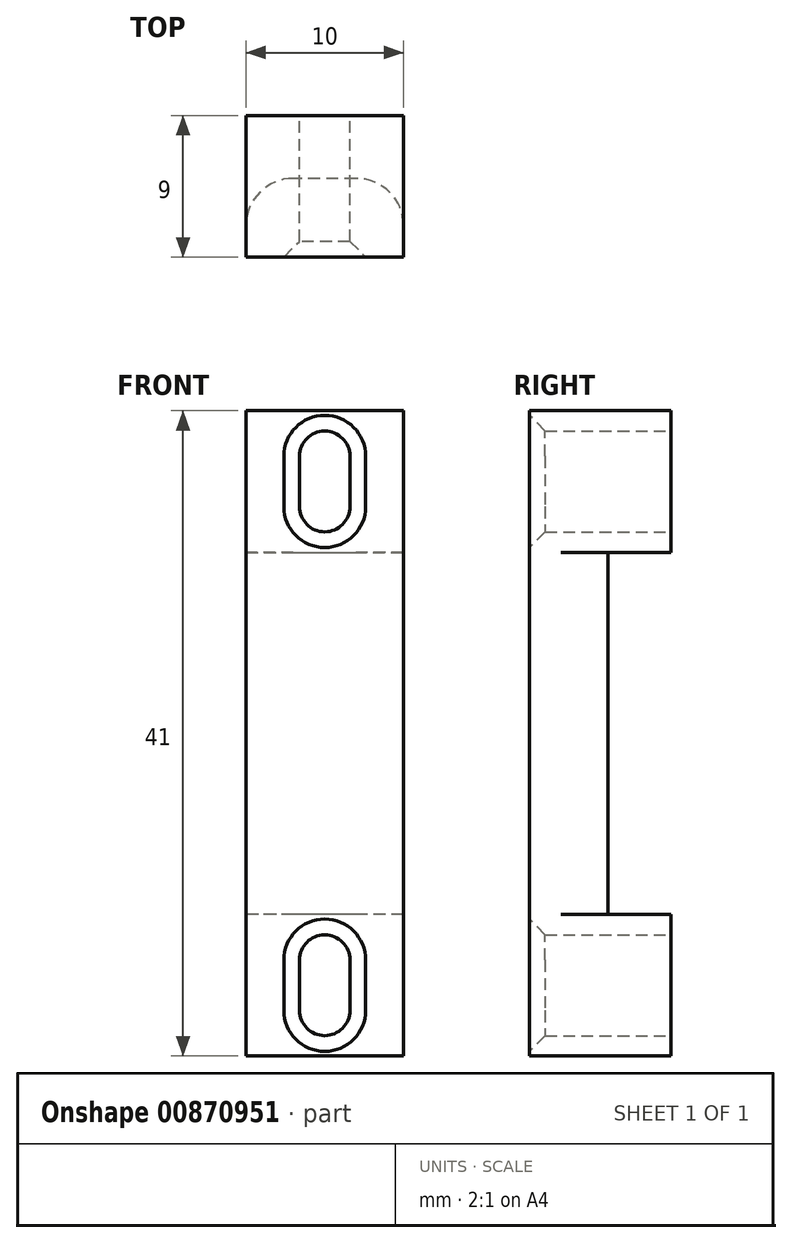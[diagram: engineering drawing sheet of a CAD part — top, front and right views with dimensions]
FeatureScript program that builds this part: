
annotation { "Feature Type Name" : "Feature", "Feature Type Description" : "" }
export const myFeature = defineFeature(function(context is Context, id is Id, definition is map)
    precondition{}
    {
        {
            var Q0;
            Q0=qCreatedBy(makeId("Front.planeOp"),FACE);
            var sketch = newSketch(context, id + "F0", { "sketchPlane" : qUnion([Q0])});
            skLineSegment(sketch, "E0.bottom", {"start": v(0, 0) * mm, "end": v(10, 0) * mm});
            skLineSegment(sketch, "E0.top", {"start": v(0, 41) * mm, "end": v(10, 41) * mm});
            skLineSegment(sketch, "E0.left", {"start": v(0, 0) * mm, "end": v(0, 41) * mm});
            skLineSegment(sketch, "E0.right", {"start": v(10, 0) * mm, "end": v(10, 41) * mm});
            skLineSegment(sketch, "E1", {"start": v(10, 20.5) * mm, "end": v(0, 20.5) * mm, "construction": true});
            skLineSegment(sketch, "E2", {"start": v(5, 20.5) * mm, "end": v(5, 36.5) * mm, "construction": true});
            skLineSegment(sketch, "E3", {"start": v(5, 20.5) * mm, "end": v(5, 4.5) * mm, "construction": true});
            skArc(sketch, "E4", {"start": v(3.4, 34.9) * mm, "mid": v(5, 33.3) * mm, "end": v(6.6, 34.9) * mm});
            skArc(sketch, "E5", {"start": v(6.6, 38.1) * mm, "mid": v(5, 39.7) * mm, "end": v(3.4, 38.1) * mm});
            skLineSegment(sketch, "E6", {"start": v(3.4, 38.1) * mm, "end": v(3.4, 34.9) * mm});
            skLineSegment(sketch, "E7", {"start": v(6.6, 38.1) * mm, "end": v(6.6, 34.9) * mm});
            skArc(sketch, "E8", {"start": v(6.6, 6.1) * mm, "mid": v(5, 7.7) * mm, "end": v(3.4, 6.1) * mm});
            skArc(sketch, "E9", {"start": v(3.4, 2.9) * mm, "mid": v(5, 1.3) * mm, "end": v(6.6, 2.9) * mm});
            skPoint(sketch, "E9.centerSnap0", {"position": v(5, 0) * mm});
            skLineSegment(sketch, "E10", {"start": v(3.4, 6.1) * mm, "end": v(3.4, 2.9) * mm});
            skLineSegment(sketch, "E11", {"start": v(6.6, 6.1) * mm, "end": v(6.6, 2.9) * mm});
            skSolve(sketch);
        }
        {
            var Q0;
            Q0=makeQuery(id+"F0.imprint","IMPRINT",FACE,{"disambiguationData":[TD([[makeQuery(id+"F0.imprint","IMPRINT",EDGE,{"derivedFrom":sQuery(id+"F0.wireOp",EDGE,"E0.bottom")}),1.0]])]});
            extrude(context, id + "F1", {"entities" : qUnion([Q0]), "depth" : 5 * mm, "offsetDistance" : 25 * mm});
        }
        {
            var Q0;
            Q0=qCreatedBy(makeId("Top.planeOp"),FACE);
            cPlane(context, id + "F2", {"entities" : qUnion([Q0]), "cplaneType" : CPlaneType.OFFSET, "offset" : 9 * mm, "width" : 150 * mm, "height" : 150 * mm});
        }
        {
            var Q0;
            Q0=qCreatedBy(id+"F2.planeOp",FACE);
            var sketch = newSketch(context, id + "F3", { "sketchPlane" : qUnion([Q0])});
            skLineSegment(sketch, "E12.0", {"start": v(3, 0) * mm, "end": v(7, 0) * mm});
            skPoint(sketch, "E13.0", {"position": v(10, -2.5) * mm});
            skLineSegment(sketch, "E14.0", {"start": v(10, -5) * mm, "end": v(10, -3) * mm});
            skLineSegment(sketch, "E15.0", {"start": v(0, -5) * mm, "end": v(0, -3) * mm});
            skPoint(sketch, "E16.visualSharp", {"position": v(0, 0) * mm});
            skArc(sketch, "E16.filletArc", {"start": v(3, 0) * mm, "mid": v(0.88, -0.88) * mm, "end": v(0, -3) * mm});
            skPoint(sketch, "E17.visualSharp", {"position": v(10, 0) * mm});
            skArc(sketch, "E17.filletArc", {"start": v(10, -3) * mm, "mid": v(9.12, -0.88) * mm, "end": v(7, 0) * mm});
            skLineSegment(sketch, "E18", {"start": v(0, -3) * mm, "end": v(0, 0) * mm});
            skLineSegment(sketch, "E19", {"start": v(3, 0) * mm, "end": v(0, 0) * mm});
            skLineSegment(sketch, "E20", {"start": v(7, 0) * mm, "end": v(10, 0) * mm});
            skLineSegment(sketch, "E21", {"start": v(10, 0) * mm, "end": v(10, -2.5) * mm});
            skLineSegment(sketch, "E22", {"start": v(10, -2.5) * mm, "end": v(10, -3) * mm});
            skSolve(sketch);
        }
        {
            var Q0;
            Q0=qSketchRegion(id+"F3",true);
            extrude(context, id + "F4", {"entities" : qUnion([Q0]), "operationType" : NewBodyOperationType.REMOVE, "depth" : 23 * mm, "offsetDistance" : 25 * mm});
        }
        {
            var Q0;
            Q0=makeQuery(id+"F1.opExtrude","CAP_FACE",FACE,{"disambiguationData":[OSD([sQuery(id+"F0.wireOp",EDGE,"E0.bottom"),sQuery(id+"F0.wireOp",EDGE,"E0.top"),sQuery(id+"F0.wireOp",EDGE,"E0.left"),sQuery(id+"F0.wireOp",EDGE,"E0.right"),sQuery(id+"F0.wireOp",EDGE,"E4"),sQuery(id+"F0.wireOp",EDGE,"E5"),sQuery(id+"F0.wireOp",EDGE,"E6"),sQuery(id+"F0.wireOp",EDGE,"E7"),sQuery(id+"F0.wireOp",EDGE,"E8"),sQuery(id+"F0.wireOp",EDGE,"E9"),sQuery(id+"F0.wireOp",EDGE,"E10"),sQuery(id+"F0.wireOp",EDGE,"E11")])],"isStart":true});
            var sketch = newSketch(context, id + "F5", { "sketchPlane" : qUnion([Q0])});
            skLineSegment(sketch, "E23.0", {"start": v(0, 41) * mm, "end": v(-10, 41) * mm});
            skLineSegment(sketch, "E24.0", {"start": v(-10, 32) * mm, "end": v(-10, 41) * mm});
            skLineSegment(sketch, "E25.0", {"start": v(0, 32) * mm, "end": v(0, 41) * mm});
            skArc(sketch, "E26.0", {"start": v(-6.6, 38.1) * mm, "mid": v(-5, 39.7) * mm, "end": v(-3.4, 38.1) * mm});
            skArc(sketch, "E27.0", {"start": v(-3.4, 34.9) * mm, "mid": v(-5, 33.3) * mm, "end": v(-6.6, 34.9) * mm});
            skLineSegment(sketch, "E28.0", {"start": v(-6.6, 38.1) * mm, "end": v(-6.6, 34.9) * mm});
            skLineSegment(sketch, "E29.0", {"start": v(-3.4, 38.1) * mm, "end": v(-3.4, 34.9) * mm});
            skLineSegment(sketch, "E30.0", {"start": v(-10, 0) * mm, "end": v(-10, 9) * mm});
            skLineSegment(sketch, "E31.0", {"start": v(0, 0) * mm, "end": v(-10, 0) * mm});
            skLineSegment(sketch, "E32.0", {"start": v(0, 0) * mm, "end": v(0, 9) * mm});
            skArc(sketch, "E33.0", {"start": v(-6.6, 6.1) * mm, "mid": v(-5, 7.7) * mm, "end": v(-3.4, 6.1) * mm});
            skLineSegment(sketch, "E34.0", {"start": v(-3.4, 6.1) * mm, "end": v(-3.4, 2.9) * mm});
            skLineSegment(sketch, "E35.0", {"start": v(-6.6, 6.1) * mm, "end": v(-6.6, 2.9) * mm});
            skArc(sketch, "E36.0", {"start": v(-3.4, 2.9) * mm, "mid": v(-5, 1.3) * mm, "end": v(-6.6, 2.9) * mm});
            skLineSegment(sketch, "E37", {"start": v(-10, 9) * mm, "end": v(0, 9) * mm});
            skLineSegment(sketch, "E38", {"start": v(-10, 32) * mm, "end": v(0, 32) * mm});
            skSolve(sketch);
        }
        {
            var Q0;
            Q0=makeQuery(id+"F5.imprint","IMPRINT",FACE,{"disambiguationData":[TD([[makeQuery(id+"F5.imprint","IMPRINT",EDGE,{"derivedFrom":sQuery(id+"F5.wireOp",EDGE,"E23.0")}),1.0]])]});
            var Q1;
            {var subQ1=sQuery(id+"F5.wireOp",EDGE,"E30.0");Q1=makeQuery(id+"F5.imprint","IMPRINT",FACE,{"disambiguationData":[TD([[makeQuery(id+"F5.imprint","IMPRINT",EDGE,{"derivedFrom":subQ1}),-1.0]])]});}
            extrude(context, id + "F6", {"entities" : qUnion([Q0, Q1]), "operationType" : NewBodyOperationType.ADD, "depth" : 4 * mm, "offsetDistance" : 25 * mm});
        }
        {
            var Q0;
            Q0=makeQuery(id+"F1.opExtrude","CAP_EDGE",EDGE,{"disambiguationData":[OSD([sQuery(id+"F0.wireOp",EDGE,"E4")])],"isStart":false});
            var Q1;
            Q1=makeQuery(id+"F1.opExtrude","CAP_EDGE",EDGE,{"disambiguationData":[OSD([sQuery(id+"F0.wireOp",EDGE,"E9")])],"isStart":false});
            chamfer(context, id + "F7", {"entities" : qUnion([Q0, Q1]), "width" : 1 * mm, "tangentPropagation" : true});
        }
    });
